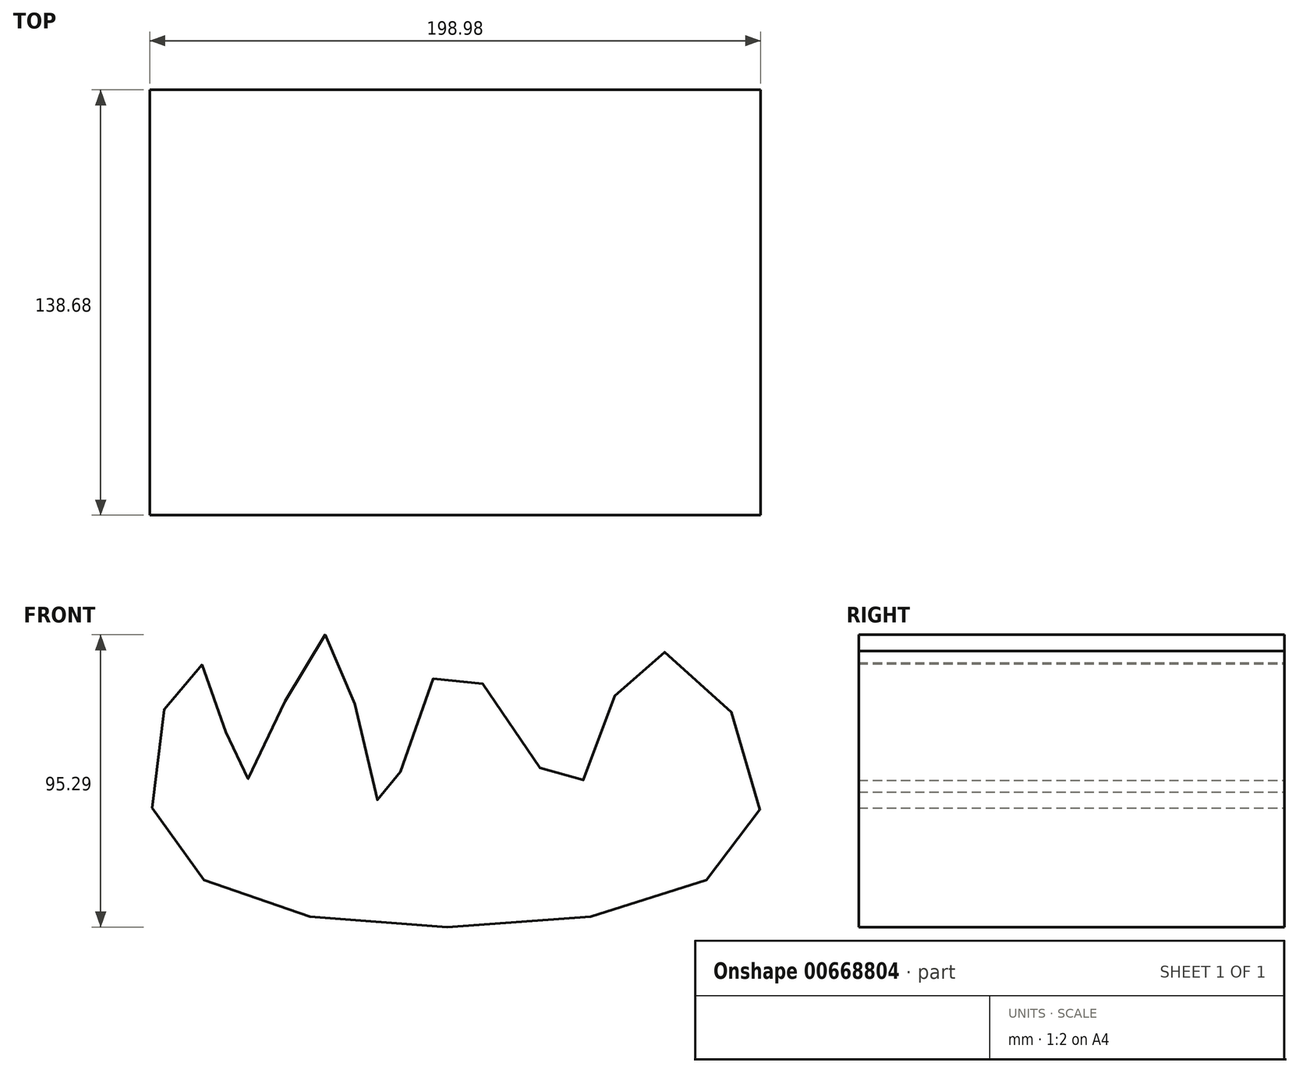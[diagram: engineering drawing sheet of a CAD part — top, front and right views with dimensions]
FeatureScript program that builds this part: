
annotation { "Feature Type Name" : "Feature", "Feature Type Description" : "" }
export const myFeature = defineFeature(function(context is Context, id is Id, definition is map)
    precondition{}
    {
        {
            var Q0;
            Q0=qCreatedBy(makeId("Front.planeOp"),FACE);
            var sketch = newSketch(context, id + "F0", { "sketchPlane" : qUnion([Q0])});
            skFitSpline(sketch, "E0", {"points": [v(-107.6, -9) * mm, v(-15.42, -47.77) * mm, v(90.51, -9.31) * mm, v(52.96, 41.36) * mm, v(27.93, -3.82) * mm, v(-10.53, 38.31) * mm, v(-32.2, -9) * mm, v(-50.83, 47.47) * mm, v(-77.39, 0) * mm, v(-90.82, 37.4) * mm, v(-107.6, -9) * mm]});
            skSolve(sketch);
        }
        {
            var Q0;
            Q0=makeQuery(id+"F0.imprint","IMPRINT",FACE,{"disambiguationData":[TD([[makeQuery(id+"F0.imprint","IMPRINT",EDGE,{"derivedFrom":sQuery(id+"F0.wireOp",EDGE,"E0")}),1.0]])]});
            extrude(context, id + "F1", {"entities" : qUnion([Q0]), "endBound" : BoundingType.SYMMETRIC, "depth" : 138.68 * mm, "offsetDistance" : 25.4 * mm});
        }
    });
